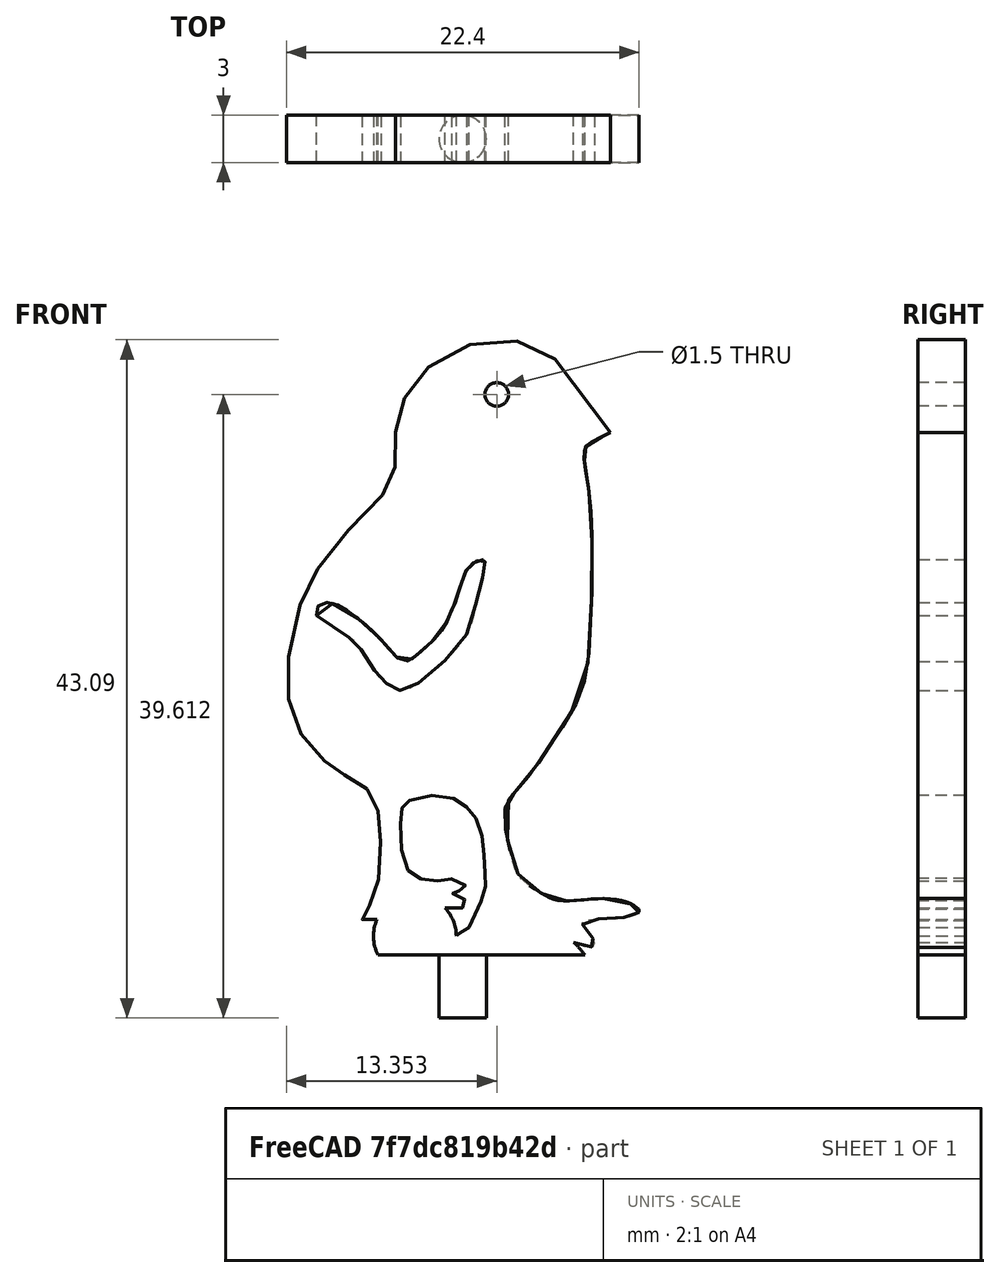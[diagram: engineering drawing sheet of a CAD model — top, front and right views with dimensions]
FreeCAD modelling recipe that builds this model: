
FCSTD DOCUMENT  (FreeCAD 0.19R)
Label: chick_1
License: All rights reserved
LicenseURL: http://en.wikipedia.org/wiki/All_rights_reserved
objects: Sketcher::SketchObject×4, PartDesign::Pad×3, Mesh::Feature×1, Part::Feature×1, PartDesign::Pocket×1, PartDesign::Body×1
note: 14 computed .brp shape members not serialized (recipe doc carries the construction recipe); baked Part::Feature solids carry a one-line shape summary decoded from their .brp

FEATURE [Mesh::Feature] chick_1
FEATURE [Part::Feature] chick_1001
  Placement = pos=(70,-1,24) rot=(0,1,0;4.71239rad)
  shape: bbox 22.5 x 1 x 38.92 mm, 2988 faces, 0 solids (baked)
FEATURE [Sketcher::SketchObject] Sketch
  FullyConstrained = false
  MapMode = 5
  Placement = pos=(0,0,0) rot=(1,0,0;1.5708rad)
  Support = -> [XZ_Plane]
  sketch-geometry (212):
    g0-g106: Circle x107 (B-spline internal-alignment scaffolding for g107; pole/knot coordinates omitted)
    g107: BSplineCurve PolesCount=107 KnotsCount=105 Degree=3 IsPeriodic=0
    g108-g211: GeomPoint x104 (B-spline internal-alignment scaffolding for g107; pole/knot coordinates omitted)
  constraints (93):
    c: Weight(g0) = 1
    c: Equal(g0, g1-g13) x13
    c: PointOnObject(g13,g12)
    c: Equal(g0, g14-g24) x11
    c: PointOnObject(g24,g23)
    c: Equal(g0,g25)
    c: PointOnObject(g25,g24)
    c: Equal(g0,g26)
    c: Equal(g0,g27)
    c: PointOnObject(g27,g26)
    c: Equal(g0, g28-g32) x5
    c: PointOnObject(g32,g31)
    c: Equal(g0,g33)
    c: PointOnObject(g33,g32)
    c: Equal(g0,g34)
    c: PointOnObject(g34,g32)
    c: Equal(g0,g35)
    c: PointOnObject(g35,g32)
    c: Equal(g0,g36)
    c: Equal(g0,g37)
    c: PointOnObject(g37,g36)
    c: Equal(g0,g38)
    c: Equal(g0,g39)
    c: PointOnObject(g39,g38)
    c: Equal(g0,g40)
    c: PointOnObject(g40,g39)
    c: Equal(g0,g41)
    c: Equal(g0,g42)
    c: PointOnObject(g42,g40)
    c: Equal(g0,g43)
    c: PointOnObject(g43,g39)
    c: Equal(g0,g44)
    c: PointOnObject(g44,g41)
    c: Equal(g0,g45)
    c: PointOnObject(g45,g41)
    c: Equal(g0,g46)
    c: PointOnObject(g46,g42)
    c: Equal(g0,g47)
    c: PointOnObject(g47,g43)
    c: Equal(g0,g48)
    c: PointOnObject(g48,g43)
    c: Equal(g0,g49)
    c: PointOnObject(g49,g48)
    c: Equal(g0,g50)
    c: Equal(g0,g51)
    c: PointOnObject(g51,g50)
    c: Equal(g0, g52-g55) x4
    c: PointOnObject(g55,g53)
    c: Equal(g0,g56)
    c: Equal(g0,g57)
    c: Equal(g0,g58)
    c: PointOnObject(g58,g57)
    c: Equal(g0,g59)
    c: Equal(g0,g60)
    c: Equal(g0,g61)
    c: PointOnObject(g61,g60)
    c: Equal(g0,g62)
    c: PointOnObject(g62,g61)
    c: Equal(g0,g63)
    c: PointOnObject(g63,g62)
    c: Equal(g0,g64)
    c: PointOnObject(g64,g63)
    c: Equal(g0,g65)
    c: PointOnObject(g65,g45)
    c: Equal(g0,g66)
    c: Equal(g0,g67)
    c: PointOnObject(g67,g40)
    c: Equal(g0,g68)
    c: Equal(g0,g69)
    c: Equal(g0,g70)
    c: PointOnObject(g70,g68)
    c: Equal(g0,g71)
    c: Equal(g0,g72)
    c: Equal(g0,g73)
    c: PointOnObject(g73,g72)
    c: Equal(g0, g74-g77) x4
    c: PointOnObject(g77,g76)
    c: Equal(g0,g78)
    c: Equal(g0,g79)
    c: PointOnObject(g79,g77)
    c: Equal(g0, g80-g89) x10
    c: PointOnObject(g89,g88)
    c: Equal(g0, g90-g101) x12
    c: PointOnObject(g101,g100)
    c: Equal(g0,g102)
    c: PointOnObject(g103,g101)
    c: Equal(g0,g104)
    c: Equal(g0,g105)
    c: Coincident(g107,g104)
    c: Equal(g0,g106)
    c: Coincident(g106,g0)
    c: InternalAlignment(g0-g106 -> g107) x107
    c: InternalAlignment(g108-g211 -> g107) x104
FEATURE [PartDesign::Pad] Pad
  Direction = (1,1,1)
  Length = 3
  Length2 = 100
  Placement = pos=(0,0,0) rot=(1,0,0;1.5708rad)
  Profile = -> Sketch
  Type = 0
FEATURE [Sketcher::SketchObject] Sketch001
  FullyConstrained = false
  MapMode = 5
  Placement = pos=(0,-3,2e-15) rot=(1,0,0;1.5708rad)
  Support = -> [Pad]
  sketch-geometry (56):
    g0: Circle CenterX=2.16297 CenterY=35.6125 CenterZ=0 NormalX=0 NormalY=0 NormalZ=1 AngleXU=0 Radius=0.75
    g1-g28: Circle x28 (B-spline internal-alignment scaffolding for g29; pole/knot coordinates omitted)
    g29: BSplineCurve PolesCount=28 KnotsCount=26 Degree=3 IsPeriodic=0
    g30-g55: GeomPoint x26 (B-spline internal-alignment scaffolding for g29; pole/knot coordinates omitted)
  constraints (27):
    c: Diameter(g0) = 1.5
    c: Weight(g1) = 1
    c: Equal(g1,g2)
    c: Equal(g1,g3)
    c: PointOnObject(g3,g2)
    c: Equal(g1,g4)
    c: Equal(g1,g5)
    c: Equal(g1,g6)
    c: PointOnObject(g6,g5)
    c: Equal(g1,g7)
    c: PointOnObject(g7,g6)
    c: Equal(g1, g8-g14) x7
    c: PointOnObject(g14,g13)
    c: Equal(g1,g15)
    c: PointOnObject(g15,g13)
    c: Equal(g1,g16)
    c: Equal(g1,g17)
    c: Equal(g1,g18)
    c: PointOnObject(g18,g17)
    c: Equal(g1,g19)
    c: PointOnObject(g19,g18)
    c: Equal(g1, g20-g27) x8
    c: PointOnObject(g27,g26)
    c: Equal(g1,g28)
    c: InternalAlignment(g1-g28 -> g29) x28
    c: InternalAlignment(g30-g55 -> g29) x26
    c: Coincident(g29,g29)
FEATURE [PartDesign::Pocket] Pocket
  BaseFeature = -> Pad
  Length = 5
  Length2 = 100
  Placement = pos=(0,0,0) rot=(1,0,0;1.5708rad)
  Profile = -> Sketch001
  Type = 0
FEATURE [Sketcher::SketchObject] Sketch002
  FullyConstrained = false
  MapMode = 5
  Placement = pos=(0,-3,3.3e-15) rot=(1,0,0;1.5708rad)
  Support = -> [Pocket]
  sketch-geometry (3):
    g0: ArcOfCircle CenterX=-3.03703 CenterY=1.18906 CenterZ=0 NormalX=0 NormalY=0 NormalZ=1 AngleXU=0 Radius=2.63225 StartAngle=0.016931 EndAngle=3.6103
    g1: ArcOfCircle CenterX=3.07329 CenterY=-3.40767 CenterZ=0 NormalX=0 NormalY=0 NormalZ=1 AngleXU=0 Radius=5.80011 StartAngle=0.627989 EndAngle=2.21395
    g2: LineSegment StartX=-5.3854 StartY=-1.3e-15 StartZ=0 EndX=7.7668 EndY=-9e-16 EndZ=0
  constraints (5):
    c: PointOnObject(g0,g-1)
    c: Coincident(g1,g0)
    c: PointOnObject(g1,g-1)
    c: Coincident(g2,g0)
    c: Coincident(g2,g1)
FEATURE [PartDesign::Pad] Pad001
  BaseFeature = -> Pocket
  Direction = (1,1,1)
  Length = 3
  Length2 = 100
  Placement = pos=(0,0,0) rot=(1,0,0;1.5708rad)
  Profile = -> Sketch002
  Reversed = true
  Type = 0
FEATURE [Sketcher::SketchObject] Sketch003
  FullyConstrained = true
  MapMode = 5
  Placement = pos=(0,0,-1.2e-15) rot=(1,0,0;3.14159rad)
  Support = -> [Pad001]
  sketch-geometry (1):
    g0: Circle CenterX=0 CenterY=1.5 CenterZ=0 NormalX=0 NormalY=0 NormalZ=1 AngleXU=0 Radius=1.5
  constraints (3):
    c: PointOnObject(g0,g-2)
    c: PointOnObject(g-1,g0)
    c: DistanceY(g-1,g0) = 1.5
FEATURE [PartDesign::Pad] Pad002
  BaseFeature = -> Pad001
  Direction = (1,1,1)
  Length = 4
  Length2 = 100
  Placement = pos=(0,0,0) rot=(1,0,0;1.5708rad)
  Profile = -> Sketch003
  Type = 0
FEATURE [PartDesign::Body] Body
  Group = -> [Sketch,Pad,Sketch001,Pocket,Sketch002,Pad001,Sketch003,Pad002]
  Origin = -> Origin
  Tip = -> Pad002
